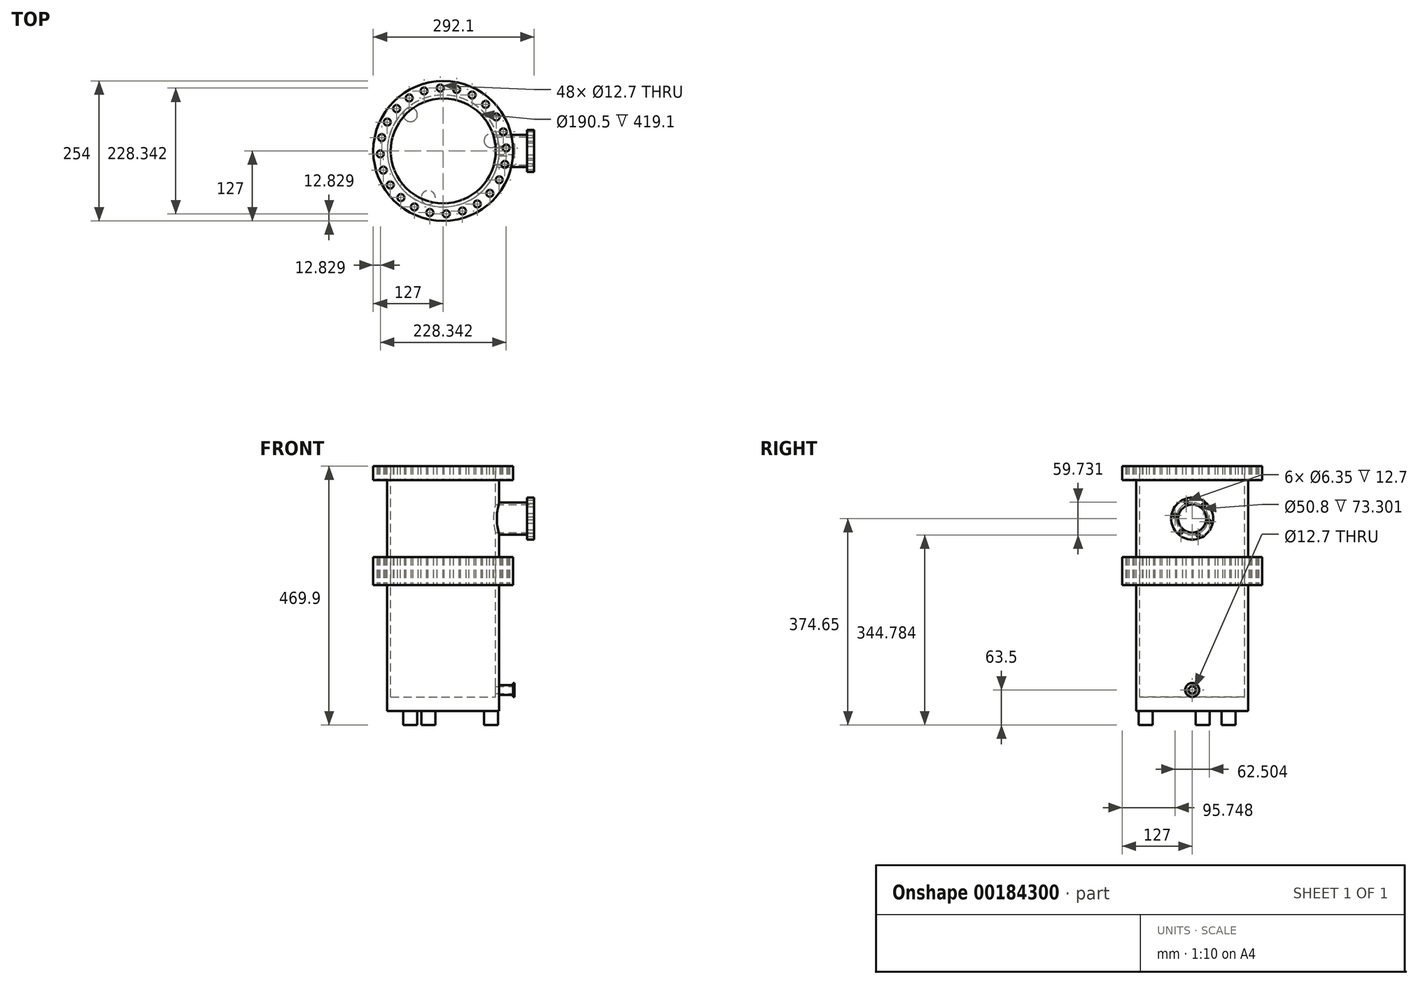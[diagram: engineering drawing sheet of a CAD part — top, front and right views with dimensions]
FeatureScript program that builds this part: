
annotation { "Feature Type Name" : "Feature", "Feature Type Description" : "" }
export const myFeature = defineFeature(function(context is Context, id is Id, definition is map)
    precondition{}
    {
        {
            var Q0;
            Q0=qCreatedBy(makeId("Top.planeOp"),FACE);
            var sketch = newSketch(context, id + "F0", { "sketchPlane" : qUnion([Q0])});
            skCircle(sketch, "E0", {"center": v(0, 0) * mm, "radius": 127 * mm});
            skCircle(sketch, "E1", {"center": v(0, 0) * mm, "radius": 101.6 * mm});
            skLineSegment(sketch, "E2", {"start": v(0, 0) * mm, "end": v(76.9, 84.57) * mm, "construction": true});
            skLineSegment(sketch, "E3.1.0", {"start": v(0, 0) * mm, "end": v(96.16, 61.78) * mm, "construction": true});
            skLineSegment(sketch, "E3.2.0", {"start": v(0, 0) * mm, "end": v(108.88, 34.79) * mm, "construction": true});
            skLineSegment(sketch, "E3.anchor1", {"start": v(0, 0) * mm, "end": v(0, 0) * mm});
            skLineSegment(sketch, "E3.anchor2", {"start": v(0, 0) * mm, "end": v(0, 0) * mm});
            skLineSegment(sketch, "E4.1.3.0", {"start": v(114.17, 5.42) * mm, "end": v(0, 0) * mm, "construction": true});
            skLineSegment(sketch, "E4.1.4.0", {"start": v(111.68, -24.31) * mm, "end": v(0, 0) * mm, "construction": true});
            skLineSegment(sketch, "E5.1.5.0", {"start": v(101.59, -52.39) * mm, "end": v(0, 0) * mm, "construction": true});
            skLineSegment(sketch, "E5.1.6.0", {"start": v(84.57, -76.9) * mm, "end": v(0, 0) * mm, "construction": true});
            skLineSegment(sketch, "E5.1.7.0", {"start": v(61.78, -96.16) * mm, "end": v(0, 0) * mm, "construction": true});
            skLineSegment(sketch, "E5.1.8.0", {"start": v(0, 0) * mm, "end": v(34.79, -108.88) * mm, "construction": true});
            skLineSegment(sketch, "E5.1.9.0", {"start": v(0, 0) * mm, "end": v(5.42, -114.17) * mm, "construction": true});
            skLineSegment(sketch, "E5.1.10.0", {"start": v(0, 0) * mm, "end": v(-24.31, -111.68) * mm, "construction": true});
            skLineSegment(sketch, "E5.1.11.0", {"start": v(0, 0) * mm, "end": v(-52.39, -101.59) * mm, "construction": true});
            skLineSegment(sketch, "E5.1.12.0", {"start": v(0, 0) * mm, "end": v(-76.9, -84.57) * mm, "construction": true});
            skLineSegment(sketch, "E5.1.13.0", {"start": v(-96.16, -61.78) * mm, "end": v(0, 0) * mm, "construction": true});
            skLineSegment(sketch, "E5.1.14.0", {"start": v(-108.88, -34.79) * mm, "end": v(0, 0) * mm, "construction": true});
            skLineSegment(sketch, "E5.1.15.0", {"start": v(-114.17, -5.42) * mm, "end": v(0, 0) * mm, "construction": true});
            skLineSegment(sketch, "E5.1.16.0", {"start": v(-111.68, 24.31) * mm, "end": v(0, 0) * mm, "construction": true});
            skLineSegment(sketch, "E5.1.17.0", {"start": v(-101.59, 52.39) * mm, "end": v(0, 0) * mm, "construction": true});
            skLineSegment(sketch, "E5.1.18.0", {"start": v(0, 0) * mm, "end": v(-84.57, 76.9) * mm, "construction": true});
            skLineSegment(sketch, "E5.1.19.0", {"start": v(0, 0) * mm, "end": v(-61.78, 96.16) * mm, "construction": true});
            skLineSegment(sketch, "E5.1.20.0", {"start": v(0, 0) * mm, "end": v(-34.79, 108.88) * mm, "construction": true});
            skLineSegment(sketch, "E5.1.21.0", {"start": v(0, 0) * mm, "end": v(-5.42, 114.17) * mm, "construction": true});
            skLineSegment(sketch, "E5.1.22.0", {"start": v(0, 0) * mm, "end": v(24.31, 111.68) * mm, "construction": true});
            skLineSegment(sketch, "E5.1.23.0", {"start": v(0, 0) * mm, "end": v(52.39, 101.59) * mm, "construction": true});
            skCircle(sketch, "E6", {"center": v(-61.78, 96.16) * mm, "radius": 6.35 * mm});
            skCircle(sketch, "E7.1.0", {"center": v(-34.79, 108.88) * mm, "radius": 6.35 * mm});
            skCircle(sketch, "E7.2.0", {"center": v(-5.42, 114.17) * mm, "radius": 6.35 * mm});
            skCircle(sketch, "E7.3.0", {"center": v(24.31, 111.68) * mm, "radius": 6.35 * mm});
            skCircle(sketch, "E7.4.0", {"center": v(52.39, 101.59) * mm, "radius": 6.35 * mm});
            skCircle(sketch, "E7.5.0", {"center": v(76.9, 84.57) * mm, "radius": 6.35 * mm});
            skCircle(sketch, "E7.6.0", {"center": v(96.16, 61.78) * mm, "radius": 6.35 * mm});
            skCircle(sketch, "E7.7.0", {"center": v(108.88, 34.79) * mm, "radius": 6.35 * mm});
            skCircle(sketch, "E7.8.0", {"center": v(114.17, 5.42) * mm, "radius": 6.35 * mm});
            skCircle(sketch, "E7.9.0", {"center": v(111.68, -24.31) * mm, "radius": 6.35 * mm});
            skCircle(sketch, "E7.10.0", {"center": v(101.59, -52.39) * mm, "radius": 6.35 * mm});
            skCircle(sketch, "E7.11.0", {"center": v(84.57, -76.9) * mm, "radius": 6.35 * mm});
            skCircle(sketch, "E7.12.0", {"center": v(61.78, -96.16) * mm, "radius": 6.35 * mm});
            skCircle(sketch, "E7.13.0", {"center": v(34.79, -108.88) * mm, "radius": 6.35 * mm});
            skCircle(sketch, "E7.14.0", {"center": v(5.42, -114.17) * mm, "radius": 6.35 * mm});
            skCircle(sketch, "E7.15.0", {"center": v(-24.31, -111.68) * mm, "radius": 6.35 * mm});
            skCircle(sketch, "E7.16.0", {"center": v(-52.39, -101.59) * mm, "radius": 6.35 * mm});
            skCircle(sketch, "E7.17.0", {"center": v(-76.9, -84.57) * mm, "radius": 6.35 * mm});
            skCircle(sketch, "E7.18.0", {"center": v(-96.16, -61.78) * mm, "radius": 6.35 * mm});
            skCircle(sketch, "E7.19.0", {"center": v(-108.88, -34.79) * mm, "radius": 6.35 * mm});
            skCircle(sketch, "E7.20.0", {"center": v(-114.17, -5.42) * mm, "radius": 6.35 * mm});
            skCircle(sketch, "E7.21.0", {"center": v(-111.68, 24.31) * mm, "radius": 6.35 * mm});
            skCircle(sketch, "E7.22.0", {"center": v(-101.59, 52.39) * mm, "radius": 6.35 * mm});
            skCircle(sketch, "E7.23.0", {"center": v(-84.57, 76.9) * mm, "radius": 6.35 * mm});
            skSolve(sketch);
        }
        {
            var Q0;
            Q0 = qSketchRegion(id + "F0", true);
            extrude(context, id + "F1", {"entities" : qUnion([Q0]), "depth" : 25.4 * mm});
        }
        {
            var Q0;
            Q0=makeQuery(id+"F1.opExtrude","CAP_FACE",FACE,{"disambiguationData":[OSD([sQuery(id+"F0.wireOp",EDGE,"E0"),sQuery(id+"F0.wireOp",EDGE,"E1"),sQuery(id+"F0.wireOp",EDGE,"E6"),sQuery(id+"F0.wireOp",EDGE,"E7.1.0"),sQuery(id+"F0.wireOp",EDGE,"E7.2.0"),sQuery(id+"F0.wireOp",EDGE,"E7.3.0"),sQuery(id+"F0.wireOp",EDGE,"E7.4.0"),sQuery(id+"F0.wireOp",EDGE,"E7.5.0"),sQuery(id+"F0.wireOp",EDGE,"E7.6.0"),sQuery(id+"F0.wireOp",EDGE,"E7.7.0"),sQuery(id+"F0.wireOp",EDGE,"E7.8.0"),sQuery(id+"F0.wireOp",EDGE,"E7.9.0"),sQuery(id+"F0.wireOp",EDGE,"E7.10.0"),sQuery(id+"F0.wireOp",EDGE,"E7.11.0"),sQuery(id+"F0.wireOp",EDGE,"E7.12.0"),sQuery(id+"F0.wireOp",EDGE,"E7.13.0"),sQuery(id+"F0.wireOp",EDGE,"E7.14.0"),sQuery(id+"F0.wireOp",EDGE,"E7.15.0"),sQuery(id+"F0.wireOp",EDGE,"E7.16.0"),sQuery(id+"F0.wireOp",EDGE,"E7.17.0"),sQuery(id+"F0.wireOp",EDGE,"E7.18.0"),sQuery(id+"F0.wireOp",EDGE,"E7.19.0"),sQuery(id+"F0.wireOp",EDGE,"E7.20.0"),sQuery(id+"F0.wireOp",EDGE,"E7.21.0"),sQuery(id+"F0.wireOp",EDGE,"E7.22.0"),sQuery(id+"F0.wireOp",EDGE,"E7.23.0")])],"isStart":true});
            var sketch = newSketch(context, id + "F2", { "sketchPlane" : qUnion([Q0])});
            skCircle(sketch, "E8", {"center": v(0, 0) * mm, "radius": 101.6 * mm});
            skCircle(sketch, "E9", {"center": v(0, 0) * mm, "radius": 95.25 * mm});
            skSolve(sketch);
        }
        {
            var Q0;
            Q0=makeQuery(id+"F2.imprint","IMPRINT",FACE,{"disambiguationData":[TD([[makeQuery(id+"F2.imprint","IMPRINT",EDGE,{"derivedFrom":sQuery(id+"F2.wireOp",EDGE,"E8")}),-1.0]])]});
            extrude(context, id + "F3", {"entities" : qUnion([Q0]), "operationType" : NewBodyOperationType.ADD, "depth" : 165.1 * mm, "hasSecondDirection" : true, "secondDirectionOppositeDirection" : true, "secondDirectionDepth" : 25.4 * mm});
        }
        {
            var Q0;
            Q0=makeQuery(id+"F3.opExtrude","CAP_FACE",FACE,{"disambiguationData":[OSD([sQuery(id+"F2.wireOp",EDGE,"E8"),sQuery(id+"F2.wireOp",EDGE,"E9")])],"isStart":false});
            var sketch = newSketch(context, id + "F4", { "sketchPlane" : qUnion([Q0])});
            skCircle(sketch, "E10", {"center": v(0, 0) * mm, "radius": 101.6 * mm});
            skCircle(sketch, "E11", {"center": v(0, 0) * mm, "radius": 127 * mm});
            skCircle(sketch, "E12", {"center": v(-96.16, 61.78) * mm, "radius": 6.35 * mm});
            skCircle(sketch, "E13.1.0", {"center": v(-108.88, 34.79) * mm, "radius": 6.35 * mm});
            skCircle(sketch, "E13.2.0", {"center": v(-114.17, 5.42) * mm, "radius": 6.35 * mm});
            skCircle(sketch, "E13.3.0", {"center": v(-111.68, -24.31) * mm, "radius": 6.35 * mm});
            skCircle(sketch, "E13.4.0", {"center": v(-101.59, -52.39) * mm, "radius": 6.35 * mm});
            skCircle(sketch, "E13.5.0", {"center": v(-84.57, -76.9) * mm, "radius": 6.35 * mm});
            skCircle(sketch, "E13.6.0", {"center": v(-61.78, -96.16) * mm, "radius": 6.35 * mm});
            skCircle(sketch, "E13.7.0", {"center": v(-34.79, -108.88) * mm, "radius": 6.35 * mm});
            skCircle(sketch, "E13.8.0", {"center": v(-5.42, -114.17) * mm, "radius": 6.35 * mm});
            skCircle(sketch, "E13.9.0", {"center": v(24.31, -111.68) * mm, "radius": 6.35 * mm});
            skCircle(sketch, "E13.10.0", {"center": v(52.39, -101.59) * mm, "radius": 6.35 * mm});
            skCircle(sketch, "E13.11.0", {"center": v(76.9, -84.57) * mm, "radius": 6.35 * mm});
            skCircle(sketch, "E13.12.0", {"center": v(96.16, -61.78) * mm, "radius": 6.35 * mm});
            skCircle(sketch, "E13.13.0", {"center": v(108.88, -34.79) * mm, "radius": 6.35 * mm});
            skCircle(sketch, "E13.14.0", {"center": v(114.17, -5.42) * mm, "radius": 6.35 * mm});
            skCircle(sketch, "E13.15.0", {"center": v(111.68, 24.31) * mm, "radius": 6.35 * mm});
            skCircle(sketch, "E13.16.0", {"center": v(101.59, 52.39) * mm, "radius": 6.35 * mm});
            skCircle(sketch, "E13.17.0", {"center": v(84.57, 76.9) * mm, "radius": 6.35 * mm});
            skCircle(sketch, "E13.18.0", {"center": v(61.78, 96.16) * mm, "radius": 6.35 * mm});
            skCircle(sketch, "E13.19.0", {"center": v(34.79, 108.88) * mm, "radius": 6.35 * mm});
            skCircle(sketch, "E13.20.0", {"center": v(5.42, 114.17) * mm, "radius": 6.35 * mm});
            skCircle(sketch, "E13.21.0", {"center": v(-24.31, 111.68) * mm, "radius": 6.35 * mm});
            skCircle(sketch, "E13.22.0", {"center": v(-52.39, 101.59) * mm, "radius": 6.35 * mm});
            skCircle(sketch, "E13.23.0", {"center": v(-76.9, 84.57) * mm, "radius": 6.35 * mm});
            skSolve(sketch);
        }
        {
            var Q0;
            Q0 = qSketchRegion(id + "F4", true);
            extrude(context, id + "F5", {"entities" : qUnion([Q0]), "operationType" : NewBodyOperationType.ADD, "oppositeDirection" : true, "depth" : 25.4 * mm});
        }
        {
            var Q0;
            Q0=makeQuery(id+"F5.boolean.opBoolean","MERGE",FACE,{"derivedFrom":[makeQuery(id+"F3.opExtrude","CAP_FACE",FACE,{"disambiguationData":[OSD([sQuery(id+"F2.wireOp",EDGE,"E8"),sQuery(id+"F2.wireOp",EDGE,"E9")])],"isStart":false}),makeQuery(id+"F5.opExtrude","CAP_FACE",FACE,{"disambiguationData":[OSD([sQuery(id+"F4.wireOp",EDGE,"E10"),sQuery(id+"F4.wireOp",EDGE,"E11"),sQuery(id+"F4.wireOp",EDGE,"E12"),sQuery(id+"F4.wireOp",EDGE,"E13.1.0"),sQuery(id+"F4.wireOp",EDGE,"E13.2.0"),sQuery(id+"F4.wireOp",EDGE,"E13.3.0"),sQuery(id+"F4.wireOp",EDGE,"E13.4.0"),sQuery(id+"F4.wireOp",EDGE,"E13.5.0"),sQuery(id+"F4.wireOp",EDGE,"E13.6.0"),sQuery(id+"F4.wireOp",EDGE,"E13.7.0"),sQuery(id+"F4.wireOp",EDGE,"E13.8.0"),sQuery(id+"F4.wireOp",EDGE,"E13.9.0"),sQuery(id+"F4.wireOp",EDGE,"E13.10.0"),sQuery(id+"F4.wireOp",EDGE,"E13.11.0"),sQuery(id+"F4.wireOp",EDGE,"E13.12.0"),sQuery(id+"F4.wireOp",EDGE,"E13.13.0"),sQuery(id+"F4.wireOp",EDGE,"E13.14.0"),sQuery(id+"F4.wireOp",EDGE,"E13.15.0"),sQuery(id+"F4.wireOp",EDGE,"E13.16.0"),sQuery(id+"F4.wireOp",EDGE,"E13.17.0"),sQuery(id+"F4.wireOp",EDGE,"E13.18.0"),sQuery(id+"F4.wireOp",EDGE,"E13.19.0"),sQuery(id+"F4.wireOp",EDGE,"E13.20.0"),sQuery(id+"F4.wireOp",EDGE,"E13.21.0"),sQuery(id+"F4.wireOp",EDGE,"E13.22.0"),sQuery(id+"F4.wireOp",EDGE,"E13.23.0")])],"isStart":true})]});
            var sketch = newSketch(context, id + "F6", { "sketchPlane" : qUnion([Q0])});
            skCircle(sketch, "E14", {"center": v(0, 0) * mm, "radius": 95.25 * mm});
            skCircle(sketch, "E15", {"center": v(0, 0) * mm, "radius": 127 * mm});
            skCircle(sketch, "E16", {"center": v(-96.16, 61.78) * mm, "radius": 6.35 * mm});
            skCircle(sketch, "E17.1.0", {"center": v(-108.88, 34.79) * mm, "radius": 6.35 * mm});
            skCircle(sketch, "E17.2.0", {"center": v(-114.17, 5.42) * mm, "radius": 6.35 * mm});
            skCircle(sketch, "E17.3.0", {"center": v(-111.68, -24.31) * mm, "radius": 6.35 * mm});
            skCircle(sketch, "E17.4.0", {"center": v(-101.59, -52.39) * mm, "radius": 6.35 * mm});
            skCircle(sketch, "E17.5.0", {"center": v(-84.57, -76.9) * mm, "radius": 6.35 * mm});
            skCircle(sketch, "E17.6.0", {"center": v(-61.78, -96.16) * mm, "radius": 6.35 * mm});
            skCircle(sketch, "E17.7.0", {"center": v(-34.79, -108.88) * mm, "radius": 6.35 * mm});
            skCircle(sketch, "E17.8.0", {"center": v(-5.42, -114.17) * mm, "radius": 6.35 * mm});
            skCircle(sketch, "E17.9.0", {"center": v(24.31, -111.68) * mm, "radius": 6.35 * mm});
            skCircle(sketch, "E17.10.0", {"center": v(52.39, -101.59) * mm, "radius": 6.35 * mm});
            skCircle(sketch, "E17.11.0", {"center": v(76.9, -84.57) * mm, "radius": 6.35 * mm});
            skCircle(sketch, "E17.12.0", {"center": v(96.16, -61.78) * mm, "radius": 6.35 * mm});
            skCircle(sketch, "E17.13.0", {"center": v(108.88, -34.79) * mm, "radius": 6.35 * mm});
            skCircle(sketch, "E17.14.0", {"center": v(114.17, -5.42) * mm, "radius": 6.35 * mm});
            skCircle(sketch, "E17.15.0", {"center": v(111.68, 24.31) * mm, "radius": 6.35 * mm});
            skCircle(sketch, "E17.16.0", {"center": v(101.59, 52.39) * mm, "radius": 6.35 * mm});
            skCircle(sketch, "E17.17.0", {"center": v(84.57, 76.9) * mm, "radius": 6.35 * mm});
            skCircle(sketch, "E17.18.0", {"center": v(61.78, 96.16) * mm, "radius": 6.35 * mm});
            skCircle(sketch, "E17.19.0", {"center": v(34.79, 108.88) * mm, "radius": 6.35 * mm});
            skCircle(sketch, "E17.20.0", {"center": v(5.42, 114.17) * mm, "radius": 6.35 * mm});
            skCircle(sketch, "E17.21.0", {"center": v(-24.31, 111.68) * mm, "radius": 6.35 * mm});
            skCircle(sketch, "E17.22.0", {"center": v(-52.39, 101.59) * mm, "radius": 6.35 * mm});
            skCircle(sketch, "E17.23.0", {"center": v(-76.9, 84.57) * mm, "radius": 6.35 * mm});
            skSolve(sketch);
        }
        {
            var Q0;
            Q0 = qSketchRegion(id + "F6", true);
            extrude(context, id + "F7", {"entities" : qUnion([Q0]), "operationType" : NewBodyOperationType.ADD, "depth" : 25.4 * mm});
        }
        {
            var Q0;
            Q0=makeQuery(id+"F7.opExtrude","CAP_FACE",FACE,{"disambiguationData":[OSD([sQuery(id+"F6.wireOp",EDGE,"E14"),sQuery(id+"F6.wireOp",EDGE,"E15"),sQuery(id+"F6.wireOp",EDGE,"E16"),sQuery(id+"F6.wireOp",EDGE,"E17.1.0"),sQuery(id+"F6.wireOp",EDGE,"E17.2.0"),sQuery(id+"F6.wireOp",EDGE,"E17.3.0"),sQuery(id+"F6.wireOp",EDGE,"E17.4.0"),sQuery(id+"F6.wireOp",EDGE,"E17.5.0"),sQuery(id+"F6.wireOp",EDGE,"E17.6.0"),sQuery(id+"F6.wireOp",EDGE,"E17.7.0"),sQuery(id+"F6.wireOp",EDGE,"E17.8.0"),sQuery(id+"F6.wireOp",EDGE,"E17.9.0"),sQuery(id+"F6.wireOp",EDGE,"E17.10.0"),sQuery(id+"F6.wireOp",EDGE,"E17.11.0"),sQuery(id+"F6.wireOp",EDGE,"E17.12.0"),sQuery(id+"F6.wireOp",EDGE,"E17.13.0"),sQuery(id+"F6.wireOp",EDGE,"E17.14.0"),sQuery(id+"F6.wireOp",EDGE,"E17.15.0"),sQuery(id+"F6.wireOp",EDGE,"E17.16.0"),sQuery(id+"F6.wireOp",EDGE,"E17.17.0"),sQuery(id+"F6.wireOp",EDGE,"E17.18.0"),sQuery(id+"F6.wireOp",EDGE,"E17.19.0"),sQuery(id+"F6.wireOp",EDGE,"E17.20.0"),sQuery(id+"F6.wireOp",EDGE,"E17.21.0"),sQuery(id+"F6.wireOp",EDGE,"E17.22.0"),sQuery(id+"F6.wireOp",EDGE,"E17.23.0")])],"isStart":false});
            var sketch = newSketch(context, id + "F8", { "sketchPlane" : qUnion([Q0])});
            skCircle(sketch, "E18", {"center": v(0, 0) * mm, "radius": 95.25 * mm});
            skCircle(sketch, "E19", {"center": v(0, 0) * mm, "radius": 101.6 * mm});
            skSolve(sketch);
        }
        {
            var Q0;
            Q0 = qSketchRegion(id + "F8", true);
            extrude(context, id + "F9", {"entities" : qUnion([Q0]), "operationType" : NewBodyOperationType.ADD, "depth" : 203.2 * mm});
        }
        {
            var Q0;
            Q0=makeQuery(id+"F9.opExtrude","CAP_FACE",FACE,{"disambiguationData":[OSD([sQuery(id+"F8.wireOp",EDGE,"E18"),sQuery(id+"F8.wireOp",EDGE,"E19")])],"isStart":false});
            var sketch = newSketch(context, id + "F10", { "sketchPlane" : qUnion([Q0])});
            skCircle(sketch, "E20", {"center": v(0, 0) * mm, "radius": 101.6 * mm});
            skSolve(sketch);
        }
        {
            var Q0;
            Q0 = qSketchRegion(id + "F10", true);
            extrude(context, id + "F11", {"entities" : qUnion([Q0]), "operationType" : NewBodyOperationType.ADD, "depth" : 25.4 * mm});
        }
        {
            var Q0;
            Q0=makeQuery(id+"F11.opExtrude","CAP_FACE",FACE,{"disambiguationData":[OSD([sQuery(id+"F10.wireOp",EDGE,"E20")])],"isStart":false});
            var sketch = newSketch(context, id + "F12", { "sketchPlane" : qUnion([Q0])});
            skCircle(sketch, "E21", {"center": v(-27.18, 84.65) * mm, "radius": 12.7 * mm});
            skCircle(sketch, "E22.1.0", {"center": v(-59.72, -65.87) * mm, "radius": 12.7 * mm});
            skCircle(sketch, "E22.2.0", {"center": v(86.9, -18.78) * mm, "radius": 12.7 * mm});
            skPoint(sketch, "E22.center", {"position": v(0, 0) * mm});
            skLineSegment(sketch, "E23", {"start": v(-27.18, 84.65) * mm, "end": v(-31.57, 96.57) * mm, "construction": true});
            skSolve(sketch);
        }
        {
            var Q0;
            Q0 = qSketchRegion(id + "F12", true);
            extrude(context, id + "F13", {"entities" : qUnion([Q0]), "operationType" : NewBodyOperationType.ADD, "depth" : 25.4 * mm});
        }
        {
            var Q0;
            Q0=qCreatedBy(makeId("Right.planeOp"),FACE);
            cPlane(context, id + "F14", {"entities" : qUnion([Q0]), "cplaneType" : CPlaneType.OFFSET, "offset" : 127 * mm, "width" : 152.4 * mm, "height" : 152.4 * mm});
        }
        {
            var Q0;
            Q0=qCreatedBy(id+"F14.planeOp",FACE);
            var sketch = newSketch(context, id + "F15", { "sketchPlane" : qUnion([Q0])});
            skLineSegment(sketch, "E24", {"start": v(0, 0) * mm, "end": v(0, -69.85) * mm, "construction": true});
            skCircle(sketch, "E25", {"center": v(0, -69.85) * mm, "radius": 25.4 * mm});
            skCircle(sketch, "E26", {"center": v(0, -69.85) * mm, "radius": 29.21 * mm});
            skSolve(sketch);
        }
        {
            var Q0;
            Q0 = qSketchRegion(id + "F15", true);
            extrude(context, id + "F16", {"entities" : qUnion([Q0]), "operationType" : NewBodyOperationType.ADD, "oppositeDirection" : true, "depth" : 31.75 * mm, "hasSecondDirection" : true, "secondDirectionOppositeDirection" : false, "secondDirectionDepth" : 25.4 * mm});
        }
        {
            var Q0;
            Q0=makeQuery(id+"F15.imprint","IMPRINT",FACE,{"disambiguationData":[TD([[makeQuery(id+"F15.imprint","IMPRINT",EDGE,{"derivedFrom":sQuery(id+"F15.wireOp",EDGE,"E25")}),1.0]])]});
            extrude(context, id + "F17", {"entities" : qUnion([Q0]), "operationType" : NewBodyOperationType.REMOVE, "oppositeDirection" : true, "depth" : 101.6 * mm});
        }
        {
            var Q0;
            Q0=makeQuery(id+"F16.opExtrude","CAP_FACE",FACE,{"disambiguationData":[OSD([sQuery(id+"F15.wireOp",EDGE,"E25"),sQuery(id+"F15.wireOp",EDGE,"E26")])],"isStart":true});
            var sketch = newSketch(context, id + "F18", { "sketchPlane" : qUnion([Q0])});
            skCircle(sketch, "E27", {"center": v(0, -69.85) * mm, "radius": 38.1 * mm});
            skCircle(sketch, "E28", {"center": v(0, -69.85) * mm, "radius": 25.4 * mm});
            skLineSegment(sketch, "E29", {"start": v(0, -69.85) * mm, "end": v(31.25, -75.45) * mm, "construction": true});
            skCircle(sketch, "E30", {"center": v(31.25, -75.45) * mm, "radius": 3.18 * mm});
            skCircle(sketch, "E31.1.0", {"center": v(20.48, -45.59) * mm, "radius": 3.18 * mm});
            skCircle(sketch, "E31.2.0", {"center": v(-10.78, -39.98) * mm, "radius": 3.18 * mm});
            skCircle(sketch, "E31.3.0", {"center": v(-31.25, -64.25) * mm, "radius": 3.18 * mm});
            skCircle(sketch, "E31.4.0", {"center": v(-20.48, -94.11) * mm, "radius": 3.18 * mm});
            skCircle(sketch, "E31.5.0", {"center": v(10.78, -99.72) * mm, "radius": 3.18 * mm});
            skSolve(sketch);
        }
        {
            var Q0;
            Q0 = qSketchRegion(id + "F18", true);
            extrude(context, id + "F19", {"entities" : qUnion([Q0]), "operationType" : NewBodyOperationType.ADD, "depth" : 12.7 * mm});
        }
        {
            var Q0;
            Q0=qCreatedBy(id+"F14.planeOp",FACE);
            var sketch = newSketch(context, id + "F20", { "sketchPlane" : qUnion([Q0])});
            skLineSegment(sketch, "E32", {"start": v(0, 0) * mm, "end": v(0, -381) * mm, "construction": true});
            skCircle(sketch, "E33", {"center": v(0, -381) * mm, "radius": 6.35 * mm});
            skCircle(sketch, "E34", {"center": v(0, -381) * mm, "radius": 8.9 * mm});
            skSolve(sketch);
        }
        {
            var Q0;
            Q0 = qSketchRegion(id + "F20", true);
            extrude(context, id + "F21", {"entities" : qUnion([Q0]), "operationType" : NewBodyOperationType.ADD, "oppositeDirection" : true, "depth" : 31.75 * mm});
        }
        {
            var Q0;
            Q0=makeQuery(id+"F21.opExtrude","CAP_FACE",FACE,{"disambiguationData":[OSD([sQuery(id+"F20.wireOp",EDGE,"E33"),sQuery(id+"F20.wireOp",EDGE,"E34")])],"isStart":true});
            var sketch = newSketch(context, id + "F22", { "sketchPlane" : qUnion([Q0])});
            skCircle(sketch, "E35", {"center": v(0, -381) * mm, "radius": 12.7 * mm});
            skCircle(sketch, "E36", {"center": v(0, -381) * mm, "radius": 6.35 * mm});
            skSolve(sketch);
        }
        {
            var Q0;
            Q0 = qSketchRegion(id + "F22", true);
            extrude(context, id + "F23", {"entities" : qUnion([Q0]), "operationType" : NewBodyOperationType.ADD, "depth" : 2.54 * mm});
        }
        {
            var Q0;
            Q0=makeQuery(id+"F22.imprint","IMPRINT",FACE,{"disambiguationData":[TD([[makeQuery(id+"F22.imprint","IMPRINT",EDGE,{"derivedFrom":sQuery(id+"F22.wireOp",EDGE,"E36")}),1.0]])]});
            extrude(context, id + "F24", {"entities" : qUnion([Q0]), "operationType" : NewBodyOperationType.REMOVE, "oppositeDirection" : true, "depth" : 38.1 * mm});
        }
    });
